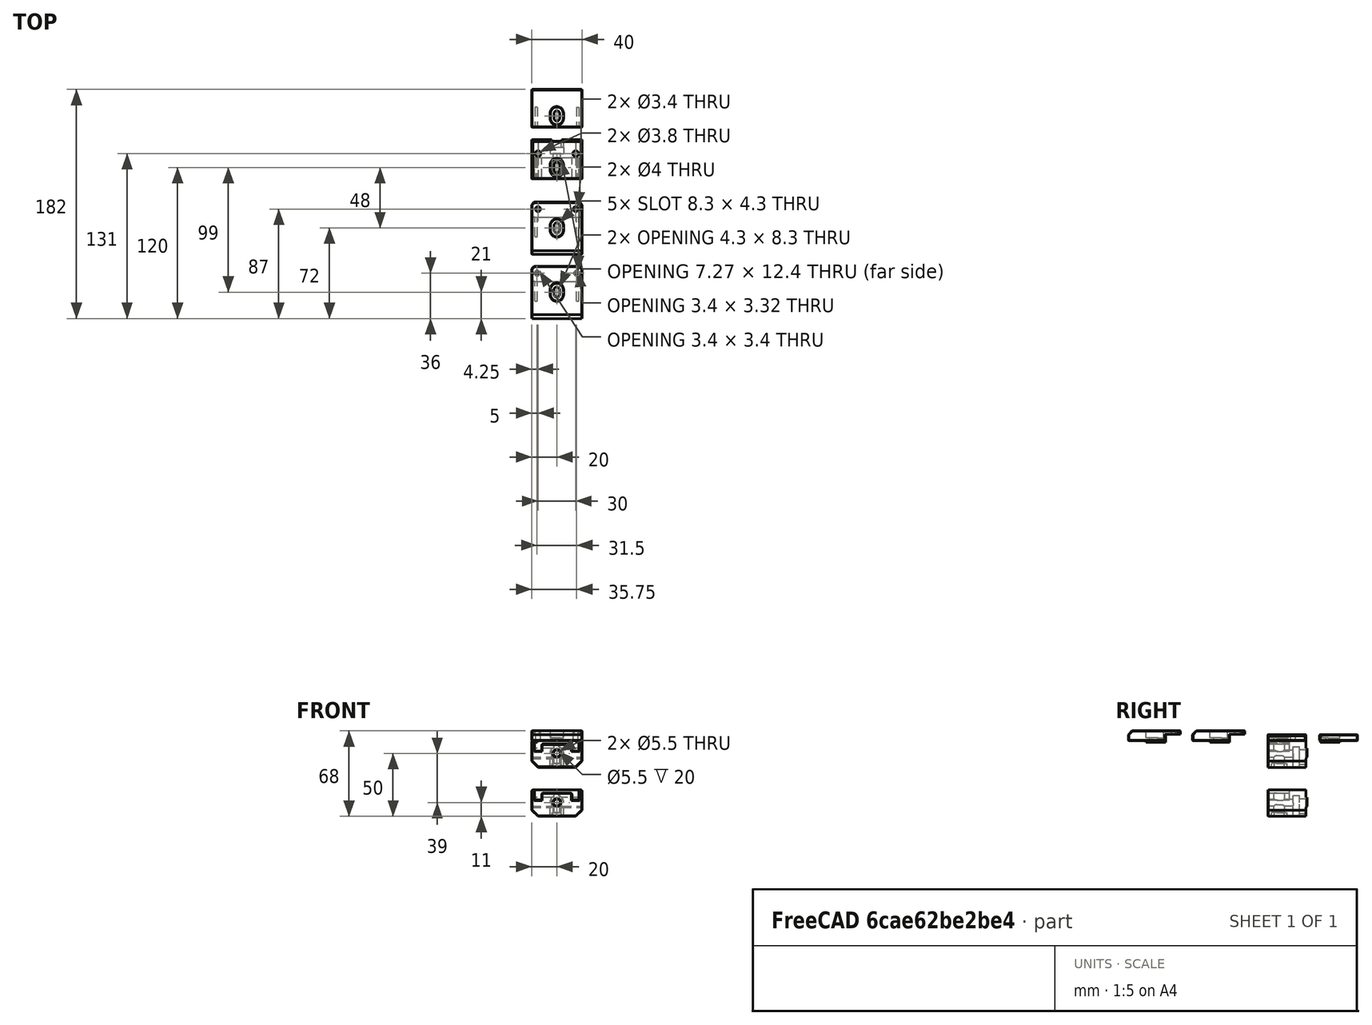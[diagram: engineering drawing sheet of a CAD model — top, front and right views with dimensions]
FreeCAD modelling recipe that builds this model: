
FCSTD DOCUMENT  (FreeCAD 0.19R24291 (Git))
Label: bottom-din-mounter
License: Other
LicenseURL: GPL3
objects: Part::Box×14, Part::MultiFuse×13, Part::Cylinder×11, Part::Feature×9, Part::Chamfer×8, Part::Cut×8, Part::Fillet×2
note: 65 computed .brp shape members not serialized (recipe doc carries the construction recipe); baked Part::Feature solids carry a one-line shape summary decoded from their .brp

FEATURE [Part::Box] Box  label="Cube"
  AttacherType = Attacher::AttachEngine3D
  Height = 25
  Length = 40
  Placement = pos=(-20,-15,0) rot=(0,0,1;0rad)
  Width = 30
FEATURE [Part::Cylinder] Cylinder
  Angle = 360
  AttacherType = Attacher::AttachEngine3D
  Height = 5
  Radius = 5.5
FEATURE [Part::Cylinder] Cylinder001
  Angle = 360
  AttacherType = Attacher::AttachEngine3D
  Height = 25
  Radius = 3.15
FEATURE [Part::MultiFuse] Fusion
  Placement = pos=(0,5,15) rot=(-1,0,0;1.5708rad)
  Shapes = -> [Cylinder001,Cylinder]
FEATURE [Part::Box] Box001  label="Cube001"
  AttacherType = Attacher::AttachEngine3D
  Height = 15
  Length = 11
  Placement = pos=(-5.5,5,0) rot=(0,0,1;0rad)
  Width = 5
FEATURE [Part::MultiFuse] Fusion001
  Shapes = -> [Fusion,Box001]
FEATURE [Part::Box] Box002  label="Cube002"
  AttacherType = Attacher::AttachEngine3D
  Height = 15
  Length = 6.3
  Placement = pos=(-3.15,10,0) rot=(0,0,1;0rad)
  Width = 20
FEATURE [Part::MultiFuse] Fusion002
  Shapes = -> [Box002,Fusion001]
FEATURE [Part::Box] Box003  label="Cube003"
  AttacherType = Attacher::AttachEngine3D
  Height = 8
  Length = 35.3
  Placement = pos=(-17.65,-15,17) rot=(0,0,1;0rad)
  Width = 17
FEATURE [Part::Box] Box004  label="Cube004"
  AttacherType = Attacher::AttachEngine3D
  Height = 5.5
  Length = 24
  Placement = pos=(-12,-15,17) rot=(0,0,1;0rad)
  Width = 17
FEATURE [Part::Box] Box005  label="Cube005"
  AttacherType = Attacher::AttachEngine3D
  Height = 8
  Length = 16
  Placement = pos=(-20,14,11) rot=(0,0,1;0rad)
  Width = 2
FEATURE [Part::Box] Box006  label="Cube006"
  AttacherType = Attacher::AttachEngine3D
  Height = 8
  Length = 16
  Placement = pos=(4,14,11) rot=(0,0,1;0rad)
  Width = 2
FEATURE [Part::MultiFuse] Fusion004
  Shapes = -> [Box006,Box005]
FEATURE [Part::Chamfer] Chamfer
  Base = -> Fusion004
  Edges = 2 edges r=1: [Edge11,Edge23]
FEATURE [Part::Cylinder] Cylinder002
  Angle = 360
  AttacherType = Attacher::AttachEngine3D
  Height = 46
  Placement = pos=(0,-22,15) rot=(-1,0,0;1.5708rad)
  Radius = 2.75
FEATURE [Part::Feature] Body001
  Placement = pos=(0,-8,0) rot=(0,0,1;1.5708rad)
  shape: bbox 7.275 x 8.4 x 10 mm, 8 faces (baked)
FEATURE [Part::Feature] Body002
  Placement = pos=(9e-16,-4,0) rot=(0,0,1;1.5708rad)
  shape: bbox 7.275 x 8.4 x 10 mm, 8 faces (baked)
FEATURE [Part::MultiFuse] Fusion006
  Placement = pos=(0,0,-3) rot=(0,0,1;0rad)
  Shapes = -> [Body002,Body001]
FEATURE [Part::Cylinder] Cylinder003
  Angle = 360
  AttacherType = Attacher::AttachEngine3D
  Height = 45
  Placement = pos=(0,-4,0) rot=(0,0,1;0rad)
  Radius = 2.15
FEATURE [Part::Cylinder] Cylinder004
  Angle = 360
  AttacherType = Attacher::AttachEngine3D
  Height = 45
  Placement = pos=(0,-8,0) rot=(0,0,1;0rad)
  Radius = 2.15
FEATURE [Part::Box] Box007  label="Cube007"
  AttacherType = Attacher::AttachEngine3D
  Height = 45
  Length = 4.3
  Placement = pos=(-2.15,-8,0) rot=(0,0,1;0rad)
  Width = 4
FEATURE [Part::MultiFuse] Fusion007
  Shapes = -> [Box007,Cylinder004,Cylinder003]
FEATURE [Part::Box] Box008  label="Cube008"
  AttacherType = Attacher::AttachEngine3D
  Height = 4
  Length = 42
  Placement = pos=(-21,-16,0) rot=(0,0,1;0rad)
  Width = 33
FEATURE [Part::Cut] Cut
  Base = -> Box
  Tool = -> Fusion002
FEATURE [Part::Cut] Cut001
  Base = -> Cut
  Tool = -> Box003
FEATURE [Part::MultiFuse] Fusion008
  Shapes = -> [Box004,Cut001]
FEATURE [Part::Cut] Cut002
  Base = -> Fusion008
  Tool = -> Cylinder002
FEATURE [Part::Cut] Cut003
  Base = -> Cut002
  Tool = -> Box008
FEATURE [Part::Cut] Cut004
  Base = -> Cut003
  Tool = -> Fusion006
FEATURE [Part::Cut] Cut005
  Base = -> Cut004
  Tool = -> Fusion007
FEATURE [Part::Chamfer] Chamfer001
  Base = -> Cut005
  Edges = 2 edges r=5: [Edge4,Edge30]
FEATURE [Part::Fillet] Fillet
  Base = -> Chamfer001
  Edges = 2 edges r=1: [Edge114,Edge115]
FEATURE [Part::Fillet] Fillet001
  Base = -> Fillet
  Edges = 2 edges r=1: [Edge55,Edge60]
FEATURE [Part::Chamfer] Chamfer002
  Base = -> Fillet001
  Edges = 2 edges r=2: [Edge31,Edge37]
FEATURE [Part::MultiFuse] Fusion009
  Shapes = -> [Chamfer,Chamfer002]
FEATURE [Part::Feature] Fusion009001  label="Fusion010"
  shape: bbox 40 x 31 x 21 mm, 54 faces (baked)
FEATURE [Part::Chamfer] Chamfer003
  Base = -> Fusion009001
  Edges = 21 edges r=0.4: [Edge44,Edge57,Edge58,Edge62,Edge63,Edge67,Edge77,Edge94,Edge97,Edge111,Edge112,Edge114,Edge116,Edge119,Edge124,Edge126,Edge131,Edge132,Edge133,Edge153,Edge154]
FEATURE [Part::Feature] Chamfer003001  label="din-end"
  Placement = pos=(0,0,-39) rot=(0,0,1;0rad)
  shape: bbox 40 x 31 x 21 mm, 75 faces (baked)
FEATURE [Part::Box] Box009  label="Cube009"
  AttacherType = Attacher::AttachEngine3D
  Height = 5
  Length = 40
  Placement = pos=(-20,-15,25) rot=(0,0,1;0rad)
  Width = 30
FEATURE [Part::Box] Box010  label="Cube010"
  AttacherType = Attacher::AttachEngine3D
  Height = 2
  Length = 1
  Placement = pos=(-17.5,-15,24) rot=(0,0,1;0rad)
  Width = 16
FEATURE [Part::Box] Box011  label="Cube011"
  AttacherType = Attacher::AttachEngine3D
  Height = 2
  Length = 1
  Placement = pos=(16.5,-15,24) rot=(0,0,1;0rad)
  Width = 16
FEATURE [Part::MultiFuse] Fusion009002
  Shapes = -> [Box011,Box010,Box009]
FEATURE [Part::Chamfer] Chamfer003002
  Base = -> Fusion009002
  Edges = 2 edges r=1: [Edge29,Edge42]
FEATURE [Part::Chamfer] Chamfer003003
  Base = -> Chamfer003002
  Edges = 2 edges r=0.4: [Edge9,Edge21]
FEATURE [Part::Cylinder] Cylinder005
  Angle = 360
  AttacherType = Attacher::AttachEngine3D
  Height = 10
  Placement = pos=(0,-4,0) rot=(0,0,1;0rad)
  Radius = 2.15
FEATURE [Part::Cylinder] Cylinder006
  Angle = 360
  AttacherType = Attacher::AttachEngine3D
  Height = 10
  Placement = pos=(0,-8,0) rot=(0,0,1;0rad)
  Radius = 2.15
FEATURE [Part::Box] Box012  label="Cube012"
  AttacherType = Attacher::AttachEngine3D
  Height = 10
  Length = 4.3
  Placement = pos=(-2.15,-8,0) rot=(0,0,1;0rad)
  Width = 4
FEATURE [Part::MultiFuse] Fusion009003
  Shapes = -> [Box012,Cylinder006,Cylinder005]
FEATURE [Part::Cylinder] Cylinder007
  Angle = 360
  AttacherType = Attacher::AttachEngine3D
  Height = 10
  Placement = pos=(0,-4,0) rot=(0,0,1;0rad)
  Radius = 5
FEATURE [Part::Cylinder] Cylinder008
  Angle = 360
  AttacherType = Attacher::AttachEngine3D
  Height = 10
  Placement = pos=(0,-8,0) rot=(0,0,1;0rad)
  Radius = 5
FEATURE [Part::Box] Box013  label="Cube013"
  AttacherType = Attacher::AttachEngine3D
  Height = 10
  Length = 10
  Placement = pos=(-5,-8,0) rot=(0,0,1;0rad)
  Width = 4
FEATURE [Part::MultiFuse] Fusion009004
  Placement = pos=(0,0,10) rot=(0,0,1;0rad)
  Shapes = -> [Cylinder007,Cylinder008,Box013]
FEATURE [Part::MultiFuse] Fusion009005
  Placement = pos=(0,0,17.5) rot=(0,0,1;0rad)
  Shapes = -> [Fusion009004,Fusion009003]
FEATURE [Part::Cut] Cut006
  Base = -> Chamfer003003
  Tool = -> Fusion009005
FEATURE [Part::Feature] Cut006001  label="Cut007"
  shape: bbox 40 x 30 x 6 mm, 27 faces (baked)
FEATURE [Part::Chamfer] Chamfer003004  label="din-cap"
  Base = -> Cut006001
  Edges = 28 edges r=0.4: [Edge1,Edge2,Edge3,Edge4,Edge5,Edge6,Edge7,Edge8,Edge9,Edge12,Edge14,Edge17,Edge18,Edge25,Edge31,Edge32,Edge33,Edge34,Edge35,Edge36,Edge38,Edge40,Edge41,Edge44,Edge51,Edge53,Edge75,Edge76]
FEATURE [Part::Feature] Cut001001  label="front"
  Placement = pos=(0,-60,25) rot=(0,0,1;0rad)
  shape: bbox 40 x 41.5 x 9 mm, 50 faces (baked)
FEATURE [Part::Feature] Chamfer005007002029002002  label="back"
  Placement = pos=(-8e-15,41,25) rot=(0,0,1;3.14159rad)
  shape: bbox 40 x 30 x 6 mm, 49 faces (baked)
FEATURE [Part::Feature] Cut001003001001  label="front-wide"
  Placement = pos=(0,-88,0) rot=(0,0,1;0rad)
  shape: bbox 40 x 41.5 x 9 mm, 50 faces (baked)
FEATURE [Part::Feature] Chamfer005007002029002003  label="back001"
  Placement = pos=(-8e-15,0,25) rot=(0,0,1;3.14159rad)
  shape: bbox 40 x 30 x 6 mm, 49 faces (baked)
FEATURE [Part::Cylinder] Cylinder009
  Angle = 360
  AttacherType = Attacher::AttachEngine3D
  Height = 10
  Placement = pos=(-15,5,21) rot=(0,0,1;0rad)
  Radius = 1.9
FEATURE [Part::Cylinder] Cylinder010
  Angle = 360
  AttacherType = Attacher::AttachEngine3D
  Height = 10
  Placement = pos=(15,5,21) rot=(0,0,1;0rad)
  Radius = 1.9
FEATURE [Part::MultiFuse] Fusion009006
  Shapes = -> [Cylinder009,Cylinder010]
FEATURE [Part::Cut] Cut001003001002
  Base = -> Chamfer005007002029002003
  Tool = -> Fusion009006
FEATURE [Part::Chamfer] Chamfer005007002029002004
  Base = -> Cut001003001002
  Edges = 4 edges r=0.4: [Edge26,Edge27,Edge47,Edge48]
